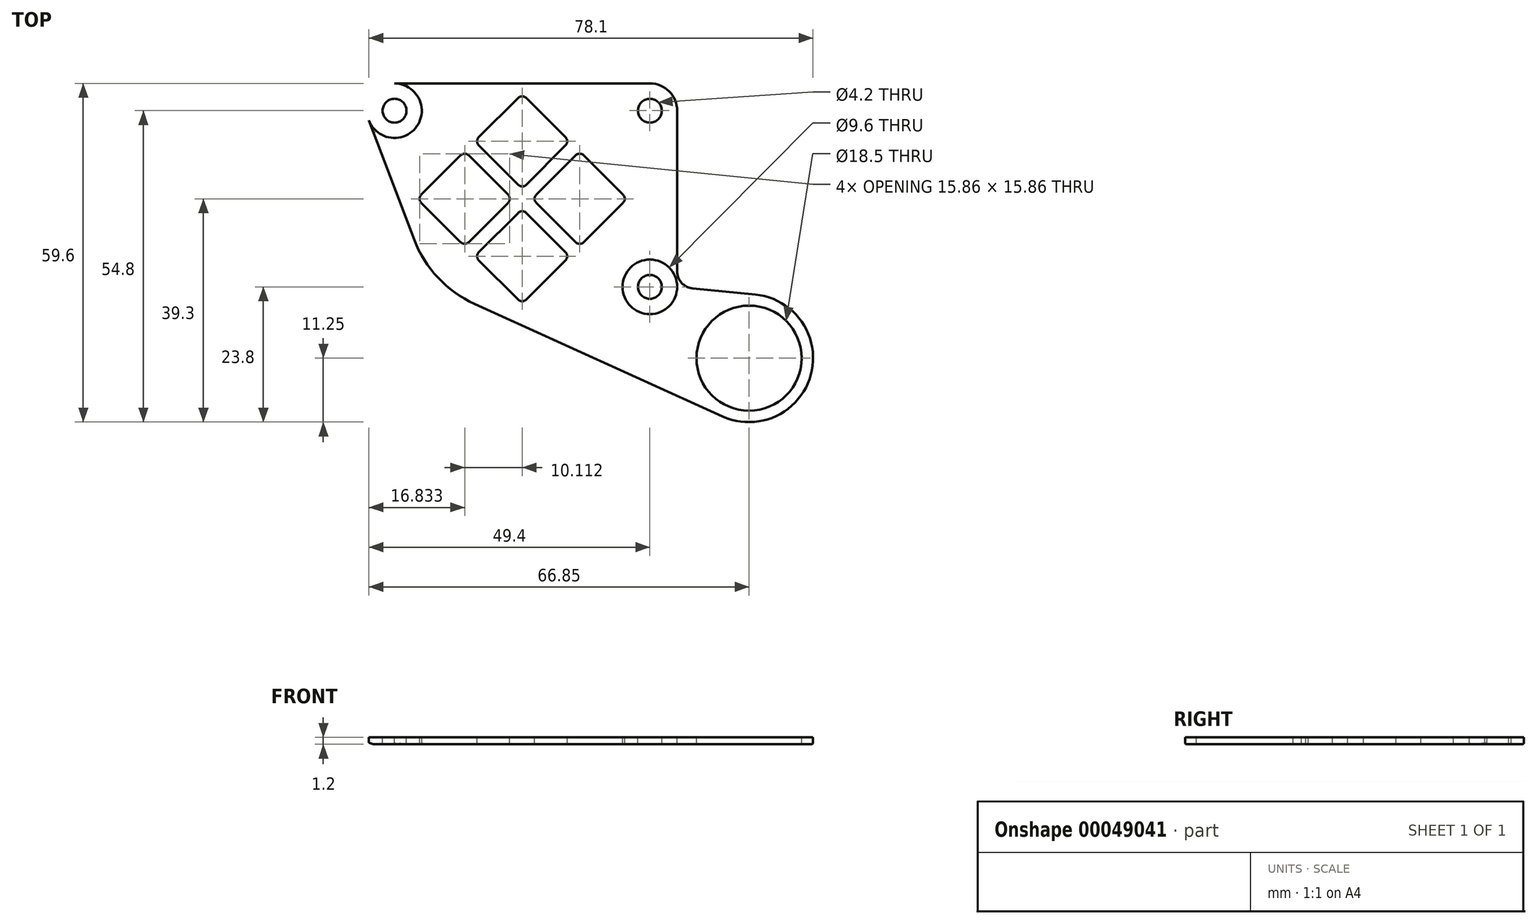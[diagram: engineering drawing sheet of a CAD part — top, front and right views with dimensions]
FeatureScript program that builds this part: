
annotation { "Feature Type Name" : "Feature", "Feature Type Description" : "" }
export const myFeature = defineFeature(function(context is Context, id is Id, definition is map)
    precondition{}
    {
        {
            var Q0;
            Q0=qCreatedBy(makeId("Top.planeOp"),FACE);
            var sketch = newSketch(context, id + "F0", { "sketchPlane" : qUnion([Q0])});
            skLineSegment(sketch, "E0", {"start": v(-41.7, 0.7) * mm, "end": v(-48.64, 7.64) * mm});
            skLineSegment(sketch, "E1", {"start": v(-50.05, 7.64) * mm, "end": v(-56.98, 0.7) * mm});
            skLineSegment(sketch, "E2", {"start": v(-56.98, -0.7) * mm, "end": v(-50.05, -7.64) * mm});
            skLineSegment(sketch, "E3", {"start": v(-41.7, -0.7) * mm, "end": v(-48.64, -7.64) * mm});
            skPoint(sketch, "E4.visualSharp", {"position": v(-49.34, 8.34) * mm});
            skArc(sketch, "E4.filletArc", {"start": v(-48.64, 7.64) * mm, "mid": v(-49.34, 7.93) * mm, "end": v(-50.05, 7.64) * mm});
            skPoint(sketch, "E5.visualSharp", {"position": v(-41, 0) * mm});
            skArc(sketch, "E5.filletArc", {"start": v(-41.7, -0.7) * mm, "mid": v(-41.41, 0) * mm, "end": v(-41.7, 0.7) * mm});
            skPoint(sketch, "E6.visualSharp", {"position": v(-49.34, -8.34) * mm});
            skArc(sketch, "E6.filletArc", {"start": v(-50.05, -7.64) * mm, "mid": v(-49.34, -7.93) * mm, "end": v(-48.64, -7.64) * mm});
            skPoint(sketch, "E7.visualSharp", {"position": v(-57.69, 0) * mm});
            skArc(sketch, "E7.filletArc", {"start": v(-56.98, 0.7) * mm, "mid": v(-57.27, 0) * mm, "end": v(-56.98, -0.7) * mm});
            skLineSegment(sketch, "E8", {"start": v(-59.46, 0) * mm, "end": v(-45.21, 14.24) * mm, "construction": true});
            skLineSegment(sketch, "E9", {"start": v(-59.46, 0) * mm, "end": v(-59.46, 17.87) * mm, "construction": true});
            skLineSegment(sketch, "E10.MirrorCS", {"start": v(-51.82, 9.4) * mm, "end": v(-58.75, 2.47) * mm});
            skArc(sketch, "E11.MirrorCS", {"start": v(-51.82, 10.82) * mm, "mid": v(-51.53, 10.11) * mm, "end": v(-51.82, 9.4) * mm});
            skArc(sketch, "E12.MirrorCS", {"start": v(-58.75, 2.47) * mm, "mid": v(-59.46, 2.18) * mm, "end": v(-60.16, 2.47) * mm});
            skLineSegment(sketch, "E13.MirrorCS", {"start": v(-60.16, 2.47) * mm, "end": v(-67.1, 9.4) * mm});
            skArc(sketch, "E14.MirrorCS", {"start": v(-67.1, 9.4) * mm, "mid": v(-67.39, 10.11) * mm, "end": v(-67.1, 10.82) * mm});
            skLineSegment(sketch, "E15.MirrorCS", {"start": v(-60.16, 17.75) * mm, "end": v(-67.1, 10.82) * mm});
            skArc(sketch, "E16.MirrorCS", {"start": v(-60.16, 17.75) * mm, "mid": v(-59.46, 18.04) * mm, "end": v(-58.75, 17.75) * mm});
            skLineSegment(sketch, "E17.MirrorCS", {"start": v(-58.75, 17.75) * mm, "end": v(-51.82, 10.82) * mm});
            skLineSegment(sketch, "E18.MirrorCS", {"start": v(-68.86, 7.64) * mm, "end": v(-61.93, 0.7) * mm});
            skArc(sketch, "E19.MirrorCS", {"start": v(-61.93, 0.7) * mm, "mid": v(-61.64, 0) * mm, "end": v(-61.93, -0.7) * mm});
            skLineSegment(sketch, "E20.MirrorCS", {"start": v(-61.93, -0.7) * mm, "end": v(-68.86, -7.64) * mm});
            skArc(sketch, "E21.MirrorCS", {"start": v(-68.86, -7.64) * mm, "mid": v(-69.57, -7.93) * mm, "end": v(-70.27, -7.64) * mm});
            skLineSegment(sketch, "E22.MirrorCS", {"start": v(-77.2, -0.7) * mm, "end": v(-70.27, -7.64) * mm});
            skArc(sketch, "E23.MirrorCS", {"start": v(-77.2, -0.7) * mm, "mid": v(-77.5, 0) * mm, "end": v(-77.2, 0.7) * mm});
            skLineSegment(sketch, "E24.MirrorCS", {"start": v(-77.2, 0.7) * mm, "end": v(-70.27, 7.64) * mm});
            skArc(sketch, "E25.MirrorCS", {"start": v(-70.27, 7.64) * mm, "mid": v(-69.57, 7.93) * mm, "end": v(-68.86, 7.64) * mm});
            skArc(sketch, "E26.MirrorCS", {"start": v(-60.16, -17.75) * mm, "mid": v(-59.46, -18.04) * mm, "end": v(-58.75, -17.75) * mm});
            skArc(sketch, "E27.MirrorCS", {"start": v(-67.1, -9.4) * mm, "mid": v(-67.39, -10.11) * mm, "end": v(-67.1, -10.82) * mm});
            skLineSegment(sketch, "E28.MirrorCS", {"start": v(-51.82, -9.4) * mm, "end": v(-58.75, -2.47) * mm});
            skLineSegment(sketch, "E29.MirrorCS", {"start": v(-60.16, -17.75) * mm, "end": v(-67.1, -10.82) * mm});
            skLineSegment(sketch, "E30.MirrorCS", {"start": v(-58.75, -17.75) * mm, "end": v(-51.82, -10.82) * mm});
            skLineSegment(sketch, "E31.MirrorCS", {"start": v(-60.16, -2.47) * mm, "end": v(-67.1, -9.4) * mm});
            skArc(sketch, "E32.MirrorCS", {"start": v(-58.75, -2.47) * mm, "mid": v(-59.46, -2.18) * mm, "end": v(-60.16, -2.47) * mm});
            skArc(sketch, "E33.MirrorCS", {"start": v(-51.82, -10.82) * mm, "mid": v(-51.53, -10.11) * mm, "end": v(-51.82, -9.4) * mm});
            skLineSegment(sketch, "E34", {"start": v(-59.46, 15.5) * mm, "end": v(0, 15.5) * mm, "construction": true});
            skLineSegment(sketch, "E35", {"start": v(-37, 15.5) * mm, "end": v(-37, 0) * mm, "construction": true});
            skCircle(sketch, "E36", {"center": v(-37, 15.5) * mm, "radius": 2.1 * mm});
            skCircle(sketch, "E37", {"center": v(-59.46, 0) * mm, "radius": 19 * mm});
            skCircle(sketch, "E38.0", {"center": v(-59.46, 0) * mm, "radius": 20.3 * mm});
            skLineSegment(sketch, "E39", {"start": v(-59.46, 20.3) * mm, "end": v(-37, 20.3) * mm});
            skCircle(sketch, "E40", {"center": v(-37, 15.5) * mm, "radius": 4.8 * mm});
            skLineSegment(sketch, "E41", {"start": v(-52.3, 19) * mm, "end": v(-40.28, 19) * mm});
            skLineSegment(sketch, "E42", {"start": v(-32.2, 15.5) * mm, "end": v(-32.2, 4.85) * mm});
            skLineSegment(sketch, "E43", {"start": v(-32.2, 0) * mm, "end": v(-33.5, 0) * mm});
            skLineSegment(sketch, "E44", {"start": v(-33.5, 0) * mm, "end": v(-33.5, 12.22) * mm});
            skLineSegment(sketch, "E45.MirrorCS", {"start": v(-32.2, -12.78) * mm, "end": v(-32.2, 0) * mm});
            skLineSegment(sketch, "E46.MirrorCS", {"start": v(-33.5, 0) * mm, "end": v(-33.5, -12.22) * mm});
            skCircle(sketch, "E47.MirrorC", {"center": v(-37, -15.5) * mm, "radius": 4.8 * mm});
            skCircle(sketch, "E48.MirrorC", {"center": v(-37, -15.5) * mm, "radius": 2.1 * mm});
            skLineSegment(sketch, "E49.MirrorCS", {"start": v(-52.3, -19) * mm, "end": v(-40.28, -19) * mm});
            skLineSegment(sketch, "E50.MirrorCS", {"start": v(-59.46, -20.3) * mm, "end": v(-37, -20.3) * mm});
            skLineSegment(sketch, "E51", {"start": v(-52.3, 19) * mm, "end": v(-59.46, 19) * mm});
            skLineSegment(sketch, "E52", {"start": v(-52.3, -19) * mm, "end": v(-59.46, -19) * mm});
            skLineSegment(sketch, "E53", {"start": v(-37, 18.05) * mm, "end": v(0, 18.05) * mm, "construction": true});
            skLineSegment(sketch, "E54", {"start": v(0, 18.05) * mm, "end": v(0, 0) * mm, "construction": true});
            skLineSegment(sketch, "E55.MirrorCS", {"start": v(-37, -18.05) * mm, "end": v(0, -18.05) * mm, "construction": true});
            skLineSegment(sketch, "E56.bottom", {"start": v(-32.05, -9.75) * mm, "end": v(-25.85, -9.75) * mm, "construction": true});
            skLineSegment(sketch, "E56.top", {"start": v(-32.05, -12.75) * mm, "end": v(-25.85, -12.75) * mm, "construction": true});
            skLineSegment(sketch, "E56.left", {"start": v(-32.05, -9.75) * mm, "end": v(-32.05, -12.75) * mm, "construction": true});
            skLineSegment(sketch, "E56.right", {"start": v(-25.85, -9.75) * mm, "end": v(-25.85, -12.75) * mm, "construction": true});
            skLineSegment(sketch, "E57", {"start": v(-39.55, 18.05) * mm, "end": v(-39.55, -18.05) * mm, "construction": true});
            skCircle(sketch, "E58", {"center": v(-19.55, -28.05) * mm, "radius": 9.25 * mm});
            skCircle(sketch, "E59.0", {"center": v(-19.55, -28.05) * mm, "radius": 11.25 * mm});
            skLineSegment(sketch, "E60", {"start": v(-24.2, -38.3) * mm, "end": v(-67.85, -18.49) * mm});
            skPoint(sketch, "E61.newPointB", {"position": v(-32.2, 0) * mm});
            skPoint(sketch, "E62.visualSharp", {"position": v(-32.65, -13.35) * mm});
            skArc(sketch, "E62.filletArc", {"start": v(-32.65, -13.17) * mm, "mid": v(-32.6, -13.3) * mm, "end": v(-32.47, -13.35) * mm});
            skPoint(sketch, "E63.visualSharp", {"position": v(-32.65, -9.15) * mm});
            skPoint(sketch, "E64.visualSharp", {"position": v(-25.25, -9.15) * mm});
            skPoint(sketch, "E65.visualSharp", {"position": v(-25.25, -13.35) * mm});
            skCircle(sketch, "E66.MirrorC", {"center": v(-81.91, 15.5) * mm, "radius": 4.8 * mm});
            skCircle(sketch, "E67.MirrorC", {"center": v(-81.91, 15.5) * mm, "radius": 2.1 * mm});
            skLineSegment(sketch, "E68", {"start": v(-86.4, 13.8) * mm, "end": v(-78.44, -7.2) * mm});
            skLineSegment(sketch, "E69", {"start": v(-81.91, 20.3) * mm, "end": v(-59.46, 20.3) * mm});
            skLineSegment(sketch, "E70", {"start": v(-32.2, 0) * mm, "end": v(-32.2, 15.5) * mm});
            skLineSegment(sketch, "E71", {"start": v(-29.5, -15.77) * mm, "end": v(-18.45, -16.85) * mm});
            skPoint(sketch, "E72.visualSharp", {"position": v(-32.2, -15.5) * mm});
            skArc(sketch, "E72.filletArc", {"start": v(-32.2, -12.78) * mm, "mid": v(-31.42, -14.8) * mm, "end": v(-29.5, -15.77) * mm});
            skSolve(sketch);
        }
        {
            var Q0;
            Q0=makeQuery(id+"F0.imprint","IMPRINT",FACE,{"disambiguationData":[TD([[makeQuery(id+"F0.imprint","IMPRINT",EDGE,{"derivedFrom":sQuery(id+"F0.wireOp",EDGE,"E67.MirrorC")}),1.0]])]});
            var Q1;
            {var subQ2=sQuery(id+"F0.wireOp",EDGE,"E68");Q1=makeQuery(id+"F0.imprint","IMPRINT",FACE,{"disambiguationData":[TD([[makeQuery(id+"F0.imprint","IMPRINT",EDGE,{"derivedFrom":subQ2}),1.0]])]});}
            var Q2;
            Q2=makeQuery(id+"F0.imprint","IMPRINT",FACE,{"disambiguationData":[TD([[makeQuery(id+"F0.imprint","IMPRINT",EDGE,{"derivedFrom":sQuery(id+"F0.wireOp",EDGE,"E0")}),-1.0]])]});
            var Q3;
            {var subQ1=sQuery(id+"F0.wireOp",EDGE,"E41");Q3=makeQuery(id+"F0.imprint","IMPRINT",FACE,{"disambiguationData":[TD([[makeQuery(id+"F0.imprint","IMPRINT",EDGE,{"derivedFrom":subQ1}),-1.0]])]});}
            var Q4;
            {var subQ0=sQuery(id+"F0.wireOp",EDGE,"E51");Q4=makeQuery(id+"F0.imprint","IMPRINT",FACE,{"disambiguationData":[TD([[makeQuery(id+"F0.imprint","IMPRINT",EDGE,{"derivedFrom":subQ0}),1.0]])]});}
            var Q5;
            {var subQ5=sQuery(id+"F0.wireOp",EDGE,"E51");Q5=makeQuery(id+"F0.imprint","IMPRINT",FACE,{"disambiguationData":[TD([[makeQuery(id+"F0.imprint","IMPRINT",EDGE,{"derivedFrom":subQ5}),-1.0]])]});}
            var Q6;
            {var subQ0=sQuery(id+"F0.wireOp",EDGE,"E39");Q6=makeQuery(id+"F0.imprint","IMPRINT",FACE,{"disambiguationData":[TD([[makeQuery(id+"F0.imprint","IMPRINT",EDGE,{"derivedFrom":subQ0}),-1.0]])]});}
            var Q7;
            Q7=makeQuery(id+"F0.imprint","IMPRINT",FACE,{"disambiguationData":[TD([[makeQuery(id+"F0.imprint","IMPRINT",EDGE,{"derivedFrom":sQuery(id+"F0.wireOp",EDGE,"E36")}),-1.0]])]});
            var Q8;
            {var subQ4=sQuery(id+"F0.wireOp",EDGE,"E43");Q8=makeQuery(id+"F0.imprint","IMPRINT",FACE,{"disambiguationData":[TD([[makeQuery(id+"F0.imprint","IMPRINT",EDGE,{"derivedFrom":subQ4}),-1.0]])]});}
            var Q9;
            Q9=makeQuery(id+"F0.imprint","IMPRINT",FACE,{"disambiguationData":[TD([[makeQuery(id+"F0.imprint","IMPRINT",EDGE,{"derivedFrom":sQuery(id+"F0.wireOp",EDGE,"E48.MirrorC")}),1.0]])]});
            var Q10;
            {var subQ0=sQuery(id+"F0.wireOp",EDGE,"E49.MirrorCS");Q10=makeQuery(id+"F0.imprint","IMPRINT",FACE,{"disambiguationData":[TD([[makeQuery(id+"F0.imprint","IMPRINT",EDGE,{"derivedFrom":subQ0}),-1.0]])]});}
            var Q11;
            Q11=makeQuery(id+"F0.imprint","IMPRINT",FACE,{"disambiguationData":[TD([[makeQuery(id+"F0.imprint","IMPRINT",EDGE,{"derivedFrom":sQuery(id+"F0.wireOp",EDGE,"E43")}),1.0]])]});
            var Q12;
            Q12=makeQuery(id+"F0.imprint","IMPRINT",FACE,{"disambiguationData":[TD([[makeQuery(id+"F0.imprint","IMPRINT",EDGE,{"derivedFrom":sQuery(id+"F0.wireOp",EDGE,"E58")}),-1.0]])]});
            extrude(context, id + "F1", {"entities" : qUnion([Q0, Q1, Q2, Q3, Q4, Q5, Q6, Q7, Q8, Q9, Q10, Q11, Q12]), "oppositeDirection" : true, "depth" : 1.2 * mm});
        }
        {
            var Q0;
            Q0=makeQuery(id+"F1.opExtrude","CAP_EDGE",EDGE,{"disambiguationData":[OSD([sQuery(id+"F0.wireOp",EDGE,"E60")])],"isStart":false});
            var Q1;
            Q1=makeQuery(id+"F1.opExtrude","CAP_EDGE",EDGE,{"disambiguationData":[OSD([sQuery(id+"F0.wireOp",EDGE,"E38.0")])],"isStart":false});
            var Q2;
            Q2=makeQuery(id+"F1.opExtrude","CAP_EDGE",EDGE,{"disambiguationData":[OSD([sQuery(id+"F0.wireOp",EDGE,"E68")])],"isStart":false});
            var Q3;
            Q3=makeQuery(id+"F1.opExtrude","CAP_EDGE",EDGE,{"disambiguationData":[OSD([sQuery(id+"F0.wireOp",EDGE,"E66.MirrorC")])],"isStart":false});
            var Q4;
            Q4=makeQuery(id+"F1.opExtrude","CAP_EDGE",EDGE,{"disambiguationData":[OSD([sQuery(id+"F0.wireOp",EDGE,"E39"),sQuery(id+"F0.wireOp",EDGE,"E69")])],"isStart":false});
            var Q5;
            Q5=makeQuery(id+"F1.opExtrude","CAP_EDGE",EDGE,{"disambiguationData":[OSD([sQuery(id+"F0.wireOp",EDGE,"E40")])],"isStart":false});
            var Q6;
            Q6=makeQuery(id+"F1.opExtrude","CAP_EDGE",EDGE,{"disambiguationData":[OSD([sQuery(id+"F0.wireOp",EDGE,"E45.MirrorCS"),sQuery(id+"F0.wireOp",EDGE,"E70")])],"isStart":false});
            var Q7;
            Q7=makeQuery(id+"F1.opExtrude","CAP_EDGE",EDGE,{"disambiguationData":[OSD([sQuery(id+"F0.wireOp",EDGE,"E72.filletArc")])],"isStart":false});
            var Q8;
            Q8=makeQuery(id+"F1.opExtrude","CAP_EDGE",EDGE,{"disambiguationData":[OSD([sQuery(id+"F0.wireOp",EDGE,"E71")])],"isStart":false});
            var Q9;
            Q9=makeQuery(id+"F1.opExtrude","CAP_EDGE",EDGE,{"disambiguationData":[OSD([sQuery(id+"F0.wireOp",EDGE,"E59.0")])],"isStart":false});
            fillet(context, id + "F2", {"entities" : qUnion([Q0, Q1, Q2, Q3, Q4, Q5, Q6, Q7, Q8, Q9]), "radius" : .3 * mm, "tangentPropagation" : true, "allowEdgeOverflow" : false});
        }
    });
